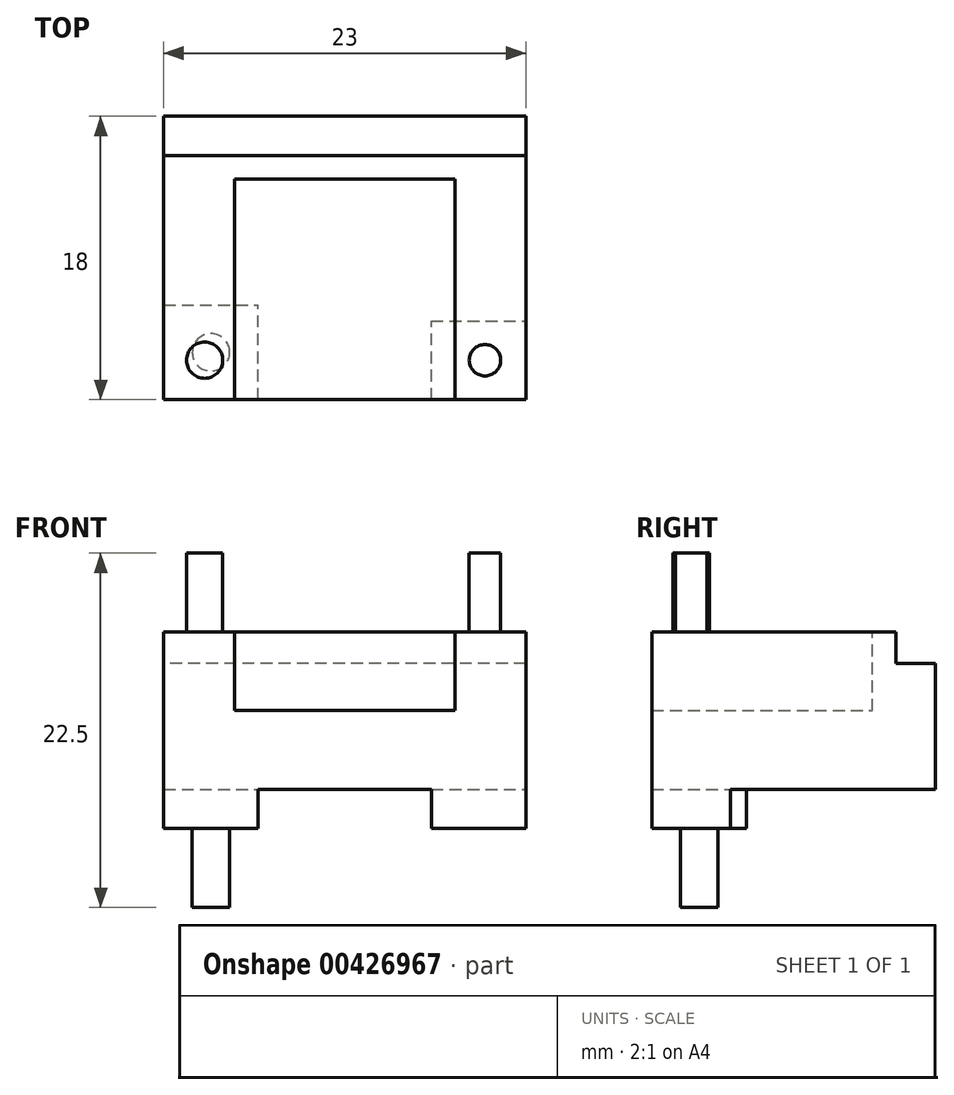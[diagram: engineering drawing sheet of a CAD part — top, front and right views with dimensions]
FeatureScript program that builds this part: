
annotation { "Feature Type Name" : "Feature", "Feature Type Description" : "" }
export const myFeature = defineFeature(function(context is Context, id is Id, definition is map)
    precondition{}
    {
        {
            var Q0;
            Q0=qCreatedBy(makeId("Top.planeOp"),FACE);
            var sketch = newSketch(context, id + "F0", { "sketchPlane" : qUnion([Q0])});
            skLineSegment(sketch, "E0.bottom", {"start": v(11.5, -9) * mm, "end": v(-11.5, -9) * mm});
            skLineSegment(sketch, "E0.top", {"start": v(11.5, 9) * mm, "end": v(-11.5, 9) * mm});
            skLineSegment(sketch, "E0.left", {"start": v(11.5, -9) * mm, "end": v(11.5, 9) * mm});
            skLineSegment(sketch, "E0.right", {"start": v(-11.5, -9) * mm, "end": v(-11.5, 9) * mm});
            skPoint(sketch, "E0.middle", {"position": v(0, 0) * mm});
            skSolve(sketch);
        }
        {
            var Q0;
            Q0 = qSketchRegion(id + "F0", true);
            extrude(context, id + "F1", {"entities" : qUnion([Q0]), "depth" : 10 * mm, "offsetDistance" : 25 * mm});
        }
        {
            var Q0;
            Q0=makeQuery(id+"F1.opExtrude","CAP_FACE",FACE,{"disambiguationData":[OSD([sQuery(id+"F0.wireOp",EDGE,"E0.bottom"),sQuery(id+"F0.wireOp",EDGE,"E0.top"),sQuery(id+"F0.wireOp",EDGE,"E0.left"),sQuery(id+"F0.wireOp",EDGE,"E0.right")])],"isStart":true});
            var sketch = newSketch(context, id + "F2", { "sketchPlane" : qUnion([Q0])});
            skLineSegment(sketch, "E1.bottom", {"start": v(-11.5, 9) * mm, "end": v(-5.5, 9) * mm});
            skLineSegment(sketch, "E1.top", {"start": v(-11.5, 3) * mm, "end": v(-5.5, 3) * mm});
            skLineSegment(sketch, "E1.left", {"start": v(-11.5, 9) * mm, "end": v(-11.5, 3) * mm});
            skLineSegment(sketch, "E1.right", {"start": v(-5.5, 9) * mm, "end": v(-5.5, 3) * mm});
            skLineSegment(sketch, "E2.bottom", {"start": v(5.5, 9) * mm, "end": v(11.5, 9) * mm});
            skLineSegment(sketch, "E2.top", {"start": v(5.5, 4) * mm, "end": v(11.5, 4) * mm});
            skLineSegment(sketch, "E2.left", {"start": v(5.5, 9) * mm, "end": v(5.5, 4) * mm});
            skLineSegment(sketch, "E2.right", {"start": v(11.5, 9) * mm, "end": v(11.5, 4) * mm});
            skSolve(sketch);
        }
        {
            var Q0;
            Q0 = qSketchRegion(id + "F2", true);
            extrude(context, id + "F3", {"entities" : qUnion([Q0]), "operationType" : NewBodyOperationType.ADD, "depth" : 2.5 * mm, "offsetDistance" : 25 * mm});
        }
        {
            var Q0;
            Q0=makeQuery(id+"F3.opExtrude","CAP_FACE",FACE,{"disambiguationData":[OSD([sQuery(id+"F2.wireOp",EDGE,"E1.bottom"),sQuery(id+"F2.wireOp",EDGE,"E1.top"),sQuery(id+"F2.wireOp",EDGE,"E1.left"),sQuery(id+"F2.wireOp",EDGE,"E1.right")])],"isStart":false});
            var sketch = newSketch(context, id + "F4", { "sketchPlane" : qUnion([Q0])});
            skCircle(sketch, "E3", {"center": v(-8.5, 6) * mm, "radius": 1.19 * mm});
            skSolve(sketch);
        }
        {
            var Q0;
            Q0 = qSketchRegion(id + "F4", true);
            extrude(context, id + "F5", {"entities" : qUnion([Q0]), "operationType" : NewBodyOperationType.ADD, "depth" : 5 * mm, "offsetDistance" : 25 * mm});
        }
        {
            var Q0;
            Q0=makeQuery(id+"F1.opExtrude","CAP_FACE",FACE,{"disambiguationData":[OSD([sQuery(id+"F0.wireOp",EDGE,"E0.bottom"),sQuery(id+"F0.wireOp",EDGE,"E0.top"),sQuery(id+"F0.wireOp",EDGE,"E0.left"),sQuery(id+"F0.wireOp",EDGE,"E0.right")])],"isStart":false});
            var sketch = newSketch(context, id + "F6", { "sketchPlane" : qUnion([Q0])});
            skLineSegment(sketch, "E4.bottom", {"start": v(-7, -9) * mm, "end": v(7, -9) * mm});
            skLineSegment(sketch, "E4.top", {"start": v(-7, 5) * mm, "end": v(7, 5) * mm});
            skLineSegment(sketch, "E4.left", {"start": v(-7, -9) * mm, "end": v(-7, 5) * mm});
            skLineSegment(sketch, "E4.right", {"start": v(7, -9) * mm, "end": v(7, 5) * mm});
            skSolve(sketch);
        }
        {
            var Q0;
            Q0 = qSketchRegion(id + "F6", true);
            extrude(context, id + "F7", {"entities" : qUnion([Q0]), "operationType" : NewBodyOperationType.REMOVE, "oppositeDirection" : true, "depth" : 5 * mm, "offsetDistance" : 25 * mm});
        }
        {
            var Q0;
            Q0=makeQuery(id+"F1.opExtrude","CAP_FACE",FACE,{"disambiguationData":[OSD([sQuery(id+"F0.wireOp",EDGE,"E0.bottom"),sQuery(id+"F0.wireOp",EDGE,"E0.top"),sQuery(id+"F0.wireOp",EDGE,"E0.left"),sQuery(id+"F0.wireOp",EDGE,"E0.right")])],"isStart":false});
            var sketch = newSketch(context, id + "F8", { "sketchPlane" : qUnion([Q0])});
            skCircle(sketch, "E5", {"center": v(-8.9, -6.5) * mm, "radius": 1.15 * mm});
            skCircle(sketch, "E6", {"center": v(8.9, -6.5) * mm, "radius": 1 * mm});
            skSolve(sketch);
        }
        {
            var Q0;
            Q0 = qSketchRegion(id + "F8", true);
            extrude(context, id + "F9", {"entities" : qUnion([Q0]), "operationType" : NewBodyOperationType.ADD, "depth" : 5 * mm, "offsetDistance" : 25 * mm});
        }
        {
            var Q0;
            Q0=makeQuery(id+"F1.opExtrude","CAP_FACE",FACE,{"disambiguationData":[OSD([sQuery(id+"F0.wireOp",EDGE,"E0.bottom"),sQuery(id+"F0.wireOp",EDGE,"E0.top"),sQuery(id+"F0.wireOp",EDGE,"E0.left"),sQuery(id+"F0.wireOp",EDGE,"E0.right")])],"isStart":false});
            var sketch = newSketch(context, id + "F10", { "sketchPlane" : qUnion([Q0])});
            skLineSegment(sketch, "E7.bottom", {"start": v(-11.5, 9) * mm, "end": v(11.5, 9) * mm});
            skLineSegment(sketch, "E7.top", {"start": v(-11.5, 6.5) * mm, "end": v(11.5, 6.5) * mm});
            skLineSegment(sketch, "E7.left", {"start": v(-11.5, 9) * mm, "end": v(-11.5, 6.5) * mm});
            skLineSegment(sketch, "E7.right", {"start": v(11.5, 9) * mm, "end": v(11.5, 6.5) * mm});
            skSolve(sketch);
        }
        {
            var Q0;
            Q0 = qSketchRegion(id + "F10", true);
            extrude(context, id + "F11", {"entities" : qUnion([Q0]), "operationType" : NewBodyOperationType.REMOVE, "oppositeDirection" : true, "depth" : 2 * mm, "offsetDistance" : 25 * mm});
        }
    });
